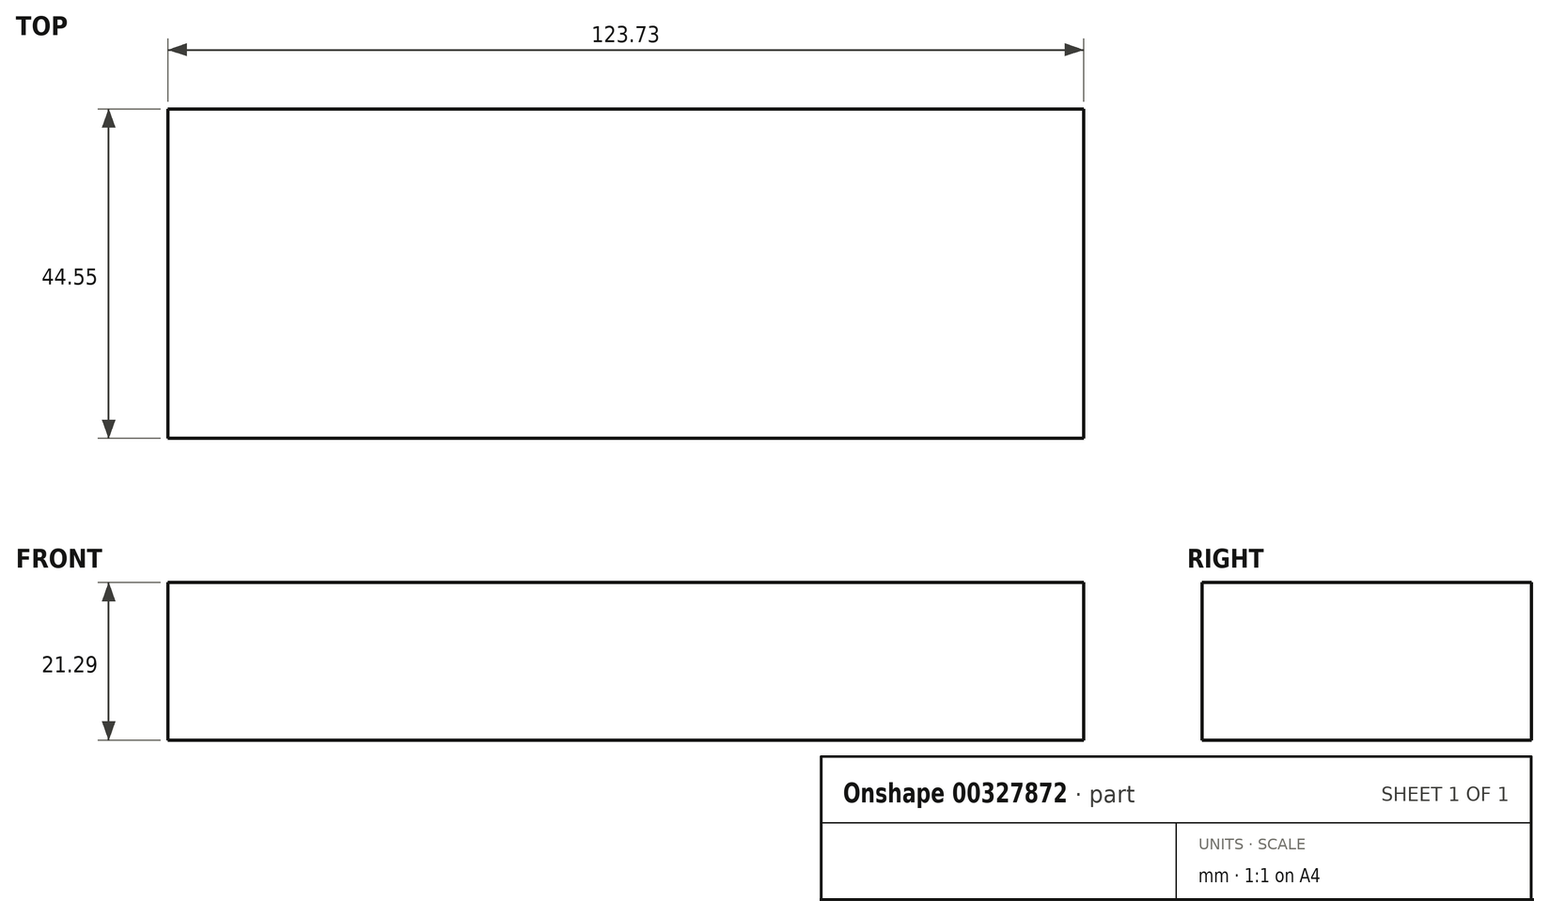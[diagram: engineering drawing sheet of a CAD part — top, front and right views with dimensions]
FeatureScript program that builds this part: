
annotation { "Feature Type Name" : "Feature", "Feature Type Description" : "" }
export const myFeature = defineFeature(function(context is Context, id is Id, definition is map)
    precondition{}
    {
        {
            var Q0;
            Q0=qCreatedBy(makeId("Top.planeOp"),FACE);
            var sketch = newSketch(context, id + "F0", { "sketchPlane" : qUnion([Q0])});
            skLineSegment(sketch, "E0.bottom", {"start": v(-61.04, 17.05) * mm, "end": v(62.7, 17.05) * mm});
            skLineSegment(sketch, "E0.top", {"start": v(-61.04, -27.5) * mm, "end": v(62.7, -27.5) * mm});
            skLineSegment(sketch, "E0.left", {"start": v(-61.04, 17.05) * mm, "end": v(-61.04, -27.5) * mm});
            skLineSegment(sketch, "E0.right", {"start": v(62.7, 17.05) * mm, "end": v(62.7, -27.5) * mm});
            skSolve(sketch);
        }
        {
            var Q0;
            Q0=makeQuery(id+"F0.imprint","IMPRINT",FACE,{"disambiguationData":[TD([[makeQuery(id+"F0.imprint","IMPRINT",EDGE,{"derivedFrom":sQuery(id+"F0.wireOp",EDGE,"E0.bottom")}),-1.0]])]});
            extrude(context, id + "F1", {"entities" : qUnion([Q0]), "depth" : 21.29 * mm});
        }
    });
